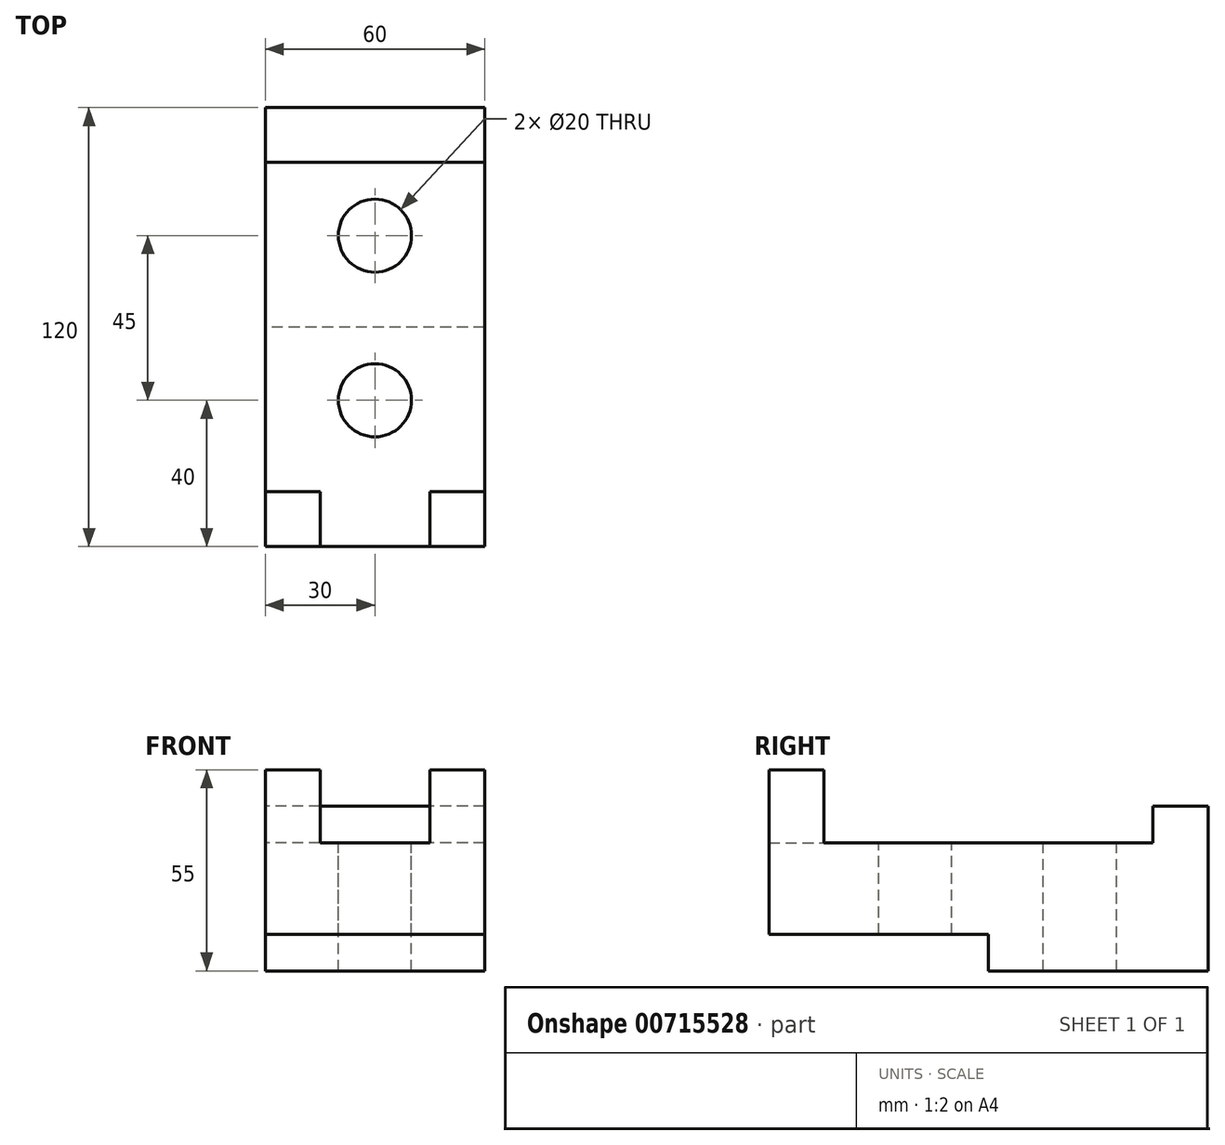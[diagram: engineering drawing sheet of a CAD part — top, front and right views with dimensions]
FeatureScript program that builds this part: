
annotation { "Feature Type Name" : "Feature", "Feature Type Description" : "" }
export const myFeature = defineFeature(function(context is Context, id is Id, definition is map)
    precondition{}
    {
        {
            var Q0;
            Q0=qCreatedBy(makeId("Top.planeOp"),FACE);
            var sketch = newSketch(context, id + "F0", { "sketchPlane" : qUnion([Q0])});
            skLineSegment(sketch, "E0.bottom", {"start": v(30, -60) * mm, "end": v(-30, -60) * mm});
            skLineSegment(sketch, "E0.top", {"start": v(30, 60) * mm, "end": v(-30, 60) * mm});
            skLineSegment(sketch, "E0.left", {"start": v(30, -60) * mm, "end": v(30, 60) * mm});
            skLineSegment(sketch, "E0.right", {"start": v(-30, -60) * mm, "end": v(-30, 60) * mm});
            skPoint(sketch, "E0.middle", {"position": v(0, 0) * mm});
            skSolve(sketch);
        }
        {
            var Q0;
            Q0 = qSketchRegion(id + "F0", true);
            extrude(context, id + "F1", {"entities" : qUnion([Q0]), "depth" : 35 * mm, "offsetDistance" : 25 * mm});
        }
        {
            var Q0;
            Q0=makeQuery(id+"F1.opExtrude","CAP_FACE",FACE,{"disambiguationData":[OSD([sQuery(id+"F0.wireOp",EDGE,"E0.bottom"),sQuery(id+"F0.wireOp",EDGE,"E0.top"),sQuery(id+"F0.wireOp",EDGE,"E0.left"),sQuery(id+"F0.wireOp",EDGE,"E0.right")])],"isStart":false});
            var sketch = newSketch(context, id + "F2", { "sketchPlane" : qUnion([Q0])});
            skLineSegment(sketch, "E1.bottom", {"start": v(30, 60) * mm, "end": v(-30, 60) * mm});
            skLineSegment(sketch, "E1.top", {"start": v(30, 45) * mm, "end": v(-30, 45) * mm});
            skLineSegment(sketch, "E1.left", {"start": v(30, 60) * mm, "end": v(30, 45) * mm});
            skLineSegment(sketch, "E1.right", {"start": v(-30, 60) * mm, "end": v(-30, 45) * mm});
            skSolve(sketch);
        }
        {
            var Q0;
            Q0=makeQuery(id+"F2.imprint","IMPRINT",FACE,{"disambiguationData":[TD([[makeQuery(id+"F2.imprint","IMPRINT",EDGE,{"derivedFrom":sQuery(id+"F2.wireOp",EDGE,"E1.bottom")}),1.0]])]});
            extrude(context, id + "F3", {"entities" : qUnion([Q0]), "operationType" : NewBodyOperationType.ADD, "depth" : 10 * mm, "offsetDistance" : 25 * mm});
        }
        {
            var Q0;
            Q0=makeQuery(id+"F1.opExtrude","CAP_FACE",FACE,{"disambiguationData":[OSD([sQuery(id+"F0.wireOp",EDGE,"E0.bottom"),sQuery(id+"F0.wireOp",EDGE,"E0.top"),sQuery(id+"F0.wireOp",EDGE,"E0.left"),sQuery(id+"F0.wireOp",EDGE,"E0.right")])],"isStart":true});
            var sketch = newSketch(context, id + "F4", { "sketchPlane" : qUnion([Q0])});
            skLineSegment(sketch, "E2.bottom", {"start": v(30, 60) * mm, "end": v(-30, 60) * mm});
            skLineSegment(sketch, "E2.top", {"start": v(30, 0) * mm, "end": v(-30, 0) * mm});
            skLineSegment(sketch, "E2.left", {"start": v(30, 60) * mm, "end": v(30, 0) * mm});
            skLineSegment(sketch, "E2.right", {"start": v(-30, 60) * mm, "end": v(-30, 0) * mm});
            skSolve(sketch);
        }
        {
            var Q0;
            Q0 = qSketchRegion(id + "F4", true);
            extrude(context, id + "F5", {"entities" : qUnion([Q0]), "operationType" : NewBodyOperationType.REMOVE, "oppositeDirection" : true, "depth" : 10 * mm, "offsetDistance" : 25 * mm});
        }
        {
            var Q0;
            Q0=makeQuery(id+"F1.opExtrude","CAP_FACE",FACE,{"disambiguationData":[OSD([sQuery(id+"F0.wireOp",EDGE,"E0.bottom"),sQuery(id+"F0.wireOp",EDGE,"E0.top"),sQuery(id+"F0.wireOp",EDGE,"E0.left"),sQuery(id+"F0.wireOp",EDGE,"E0.right")])],"isStart":false});
            var sketch = newSketch(context, id + "F6", { "sketchPlane" : qUnion([Q0])});
            skLineSegment(sketch, "E3.bottom", {"start": v(-30, -60) * mm, "end": v(-15, -60) * mm});
            skLineSegment(sketch, "E3.top", {"start": v(-30, -45) * mm, "end": v(-15, -45) * mm});
            skLineSegment(sketch, "E3.left", {"start": v(-30, -60) * mm, "end": v(-30, -45) * mm});
            skLineSegment(sketch, "E3.right", {"start": v(-15, -60) * mm, "end": v(-15, -45) * mm});
            skSolve(sketch);
        }
        {
            var Q0;
            Q0=makeQuery(id+"F6.imprint","IMPRINT",FACE,{"disambiguationData":[TD([[makeQuery(id+"F6.imprint","IMPRINT",EDGE,{"derivedFrom":sQuery(id+"F6.wireOp",EDGE,"E3.bottom")}),-1.0]])]});
            extrude(context, id + "F7", {"entities" : qUnion([Q0]), "operationType" : NewBodyOperationType.ADD, "depth" : 20 * mm, "offsetDistance" : 25 * mm});
        }
        {
            var Q0;
            Q0=makeQuery(id+"F1.opExtrude","CAP_FACE",FACE,{"disambiguationData":[OSD([sQuery(id+"F0.wireOp",EDGE,"E0.bottom"),sQuery(id+"F0.wireOp",EDGE,"E0.top"),sQuery(id+"F0.wireOp",EDGE,"E0.left"),sQuery(id+"F0.wireOp",EDGE,"E0.right")])],"isStart":false});
            var sketch = newSketch(context, id + "F8", { "sketchPlane" : qUnion([Q0])});
            skLineSegment(sketch, "E4.bottom", {"start": v(30, -60) * mm, "end": v(15, -60) * mm});
            skLineSegment(sketch, "E4.top", {"start": v(30, -45) * mm, "end": v(15, -45) * mm});
            skLineSegment(sketch, "E4.left", {"start": v(30, -60) * mm, "end": v(30, -45) * mm});
            skLineSegment(sketch, "E4.right", {"start": v(15, -60) * mm, "end": v(15, -45) * mm});
            skSolve(sketch);
        }
        {
            var Q0;
            Q0 = qSketchRegion(id + "F8", true);
            extrude(context, id + "F9", {"entities" : qUnion([Q0]), "operationType" : NewBodyOperationType.ADD, "depth" : 20 * mm, "offsetDistance" : 25 * mm});
        }
        {
            var Q0;
            Q0=makeQuery(id+"F1.opExtrude","CAP_FACE",FACE,{"disambiguationData":[OSD([sQuery(id+"F0.wireOp",EDGE,"E0.bottom"),sQuery(id+"F0.wireOp",EDGE,"E0.top"),sQuery(id+"F0.wireOp",EDGE,"E0.left"),sQuery(id+"F0.wireOp",EDGE,"E0.right")])],"isStart":false});
            var sketch = newSketch(context, id + "F10", { "sketchPlane" : qUnion([Q0])});
            skCircle(sketch, "E5", {"center": v(0, 25) * mm, "radius": 10 * mm});
            skSolve(sketch);
        }
        {
            var Q0;
            Q0=makeQuery(id+"F10.imprint","IMPRINT",FACE,{"disambiguationData":[TD([[makeQuery(id+"F10.imprint","IMPRINT",EDGE,{"derivedFrom":sQuery(id+"F10.wireOp",EDGE,"E5")}),1.0]])]});
            extrude(context, id + "F11", {"entities" : qUnion([Q0]), "operationType" : NewBodyOperationType.REMOVE, "oppositeDirection" : true, "depth" : 72.9 * mm, "offsetDistance" : 25 * mm});
        }
        {
            var Q0;
            Q0=makeQuery(id+"F1.opExtrude","CAP_FACE",FACE,{"disambiguationData":[OSD([sQuery(id+"F0.wireOp",EDGE,"E0.bottom"),sQuery(id+"F0.wireOp",EDGE,"E0.top"),sQuery(id+"F0.wireOp",EDGE,"E0.left"),sQuery(id+"F0.wireOp",EDGE,"E0.right")])],"isStart":false});
            var sketch = newSketch(context, id + "F12", { "sketchPlane" : qUnion([Q0])});
            skCircle(sketch, "E6", {"center": v(0, -20) * mm, "radius": 10 * mm});
            skSolve(sketch);
        }
        {
            var Q0;
            Q0 = qSketchRegion(id + "F12", true);
            extrude(context, id + "F13", {"entities" : qUnion([Q0]), "operationType" : NewBodyOperationType.REMOVE, "oppositeDirection" : true, "depth" : 66.7 * mm, "offsetDistance" : 25 * mm});
        }
    });
